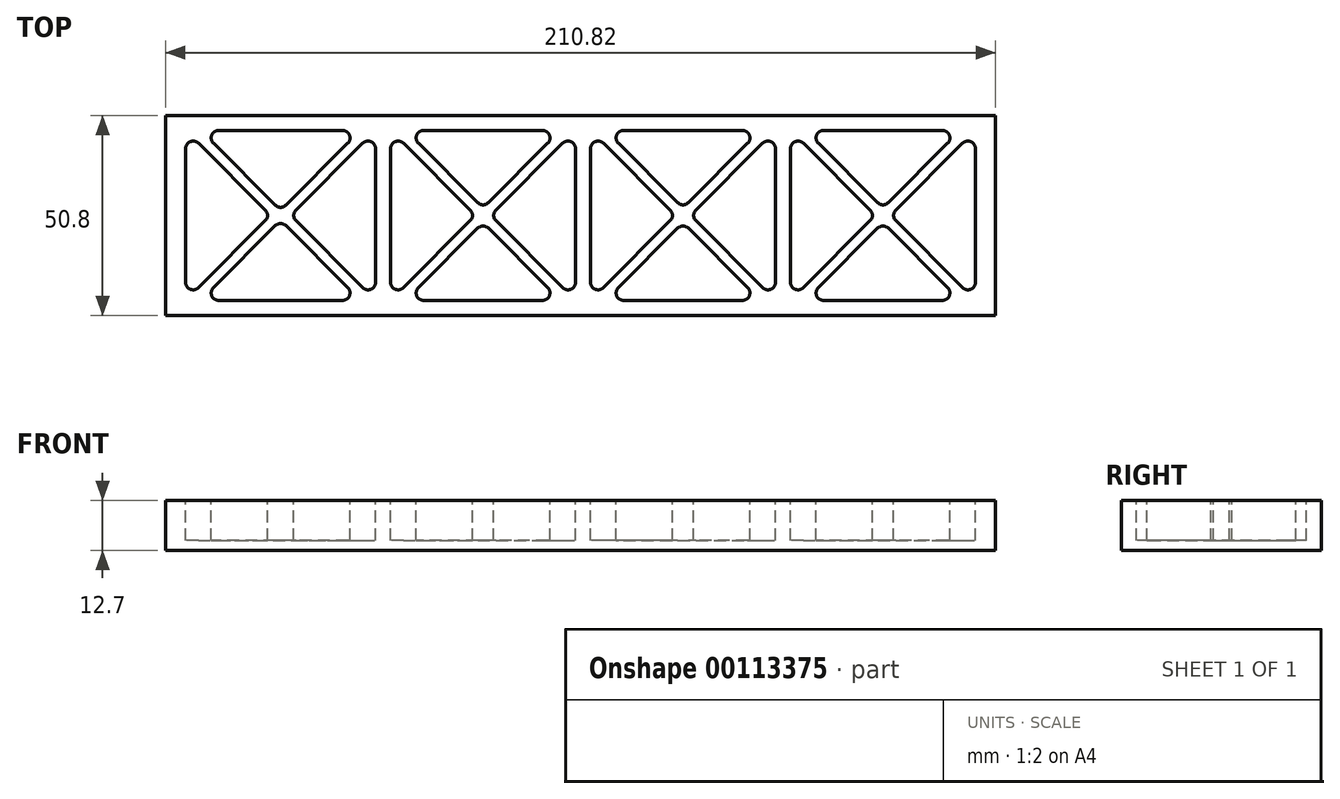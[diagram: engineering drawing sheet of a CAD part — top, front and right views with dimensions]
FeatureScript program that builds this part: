
annotation { "Feature Type Name" : "Feature", "Feature Type Description" : "" }
export const myFeature = defineFeature(function(context is Context, id is Id, definition is map)
    precondition{}
    {
        {
            var Q0;
            Q0=qCreatedBy(makeId("Top.planeOp"),FACE);
            var sketch = newSketch(context, id + "F0", { "sketchPlane" : qUnion([Q0])});
            skLineSegment(sketch, "E0.bottom", {"start": v(0, 0) * mm, "end": v(210.82, 0) * mm});
            skLineSegment(sketch, "E0.top", {"start": v(0, 50.8) * mm, "end": v(210.82, 50.8) * mm});
            skLineSegment(sketch, "E0.left", {"start": v(0, 0) * mm, "end": v(0, 50.8) * mm});
            skLineSegment(sketch, "E0.right", {"start": v(210.82, 0) * mm, "end": v(210.82, 50.8) * mm});
            skSolve(sketch);
        }
        {
            var Q0;
            Q0 = qSketchRegion(id + "F0", true);
            extrude(context, id + "F1", {"entities" : qUnion([Q0]), "depth" : 12.7 * mm, "offsetDistance" : 25.4 * mm});
        }
        {
            var Q0;
            Q0=makeQuery(id+"F1.opExtrude","CAP_FACE",FACE,{"disambiguationData":[OSD([sQuery(id+"F0.wireOp",EDGE,"E0.bottom"),sQuery(id+"F0.wireOp",EDGE,"E0.top"),sQuery(id+"F0.wireOp",EDGE,"E0.left"),sQuery(id+"F0.wireOp",EDGE,"E0.right")])],"isStart":false});
            var sketch = newSketch(context, id + "F2", { "sketchPlane" : qUnion([Q0])});
            skLineSegment(sketch, "E1", {"start": v(0, 25.4) * mm, "end": v(210.82, 25.4) * mm, "construction": true});
            skLineSegment(sketch, "E2", {"start": v(5.08, 42.4) * mm, "end": v(5.08, 8.4) * mm});
            skLineSegment(sketch, "E3", {"start": v(8.33, 7.06) * mm, "end": v(25.32, 24.05) * mm});
            skLineSegment(sketch, "E4", {"start": v(25.32, 26.75) * mm, "end": v(8.33, 43.74) * mm});
            skLineSegment(sketch, "E5", {"start": v(33.1, 26.75) * mm, "end": v(50.09, 43.74) * mm});
            skLineSegment(sketch, "E6", {"start": v(53.34, 42.4) * mm, "end": v(53.34, 8.4) * mm});
            skLineSegment(sketch, "E7", {"start": v(50.09, 7.06) * mm, "end": v(33.1, 24.05) * mm});
            skLineSegment(sketch, "E8", {"start": v(57.15, 42.4) * mm, "end": v(57.15, 8.4) * mm});
            skLineSegment(sketch, "E9", {"start": v(60.4, 7.06) * mm, "end": v(77.4, 24.05) * mm});
            skLineSegment(sketch, "E10", {"start": v(77.4, 26.75) * mm, "end": v(60.4, 43.74) * mm});
            skLineSegment(sketch, "E11", {"start": v(104.14, 42.4) * mm, "end": v(104.14, 8.4) * mm});
            skLineSegment(sketch, "E12", {"start": v(100.89, 7.06) * mm, "end": v(83.9, 24.05) * mm});
            skLineSegment(sketch, "E13", {"start": v(83.9, 26.75) * mm, "end": v(100.89, 43.74) * mm});
            skLineSegment(sketch, "E14", {"start": v(107.95, 42.4) * mm, "end": v(107.95, 8.4) * mm});
            skLineSegment(sketch, "E15", {"start": v(111.2, 7.06) * mm, "end": v(128.2, 24.05) * mm});
            skLineSegment(sketch, "E16", {"start": v(128.2, 26.75) * mm, "end": v(111.2, 43.74) * mm});
            skLineSegment(sketch, "E17", {"start": v(154.94, 42.4) * mm, "end": v(154.94, 8.4) * mm});
            skLineSegment(sketch, "E18", {"start": v(151.69, 7.06) * mm, "end": v(134.7, 24.05) * mm});
            skLineSegment(sketch, "E19", {"start": v(134.7, 26.75) * mm, "end": v(151.69, 43.74) * mm});
            skLineSegment(sketch, "E20", {"start": v(158.75, 42.4) * mm, "end": v(158.75, 8.4) * mm});
            skLineSegment(sketch, "E21", {"start": v(162, 7.06) * mm, "end": v(179, 24.05) * mm});
            skLineSegment(sketch, "E22", {"start": v(179, 26.75) * mm, "end": v(162, 43.74) * mm});
            skLineSegment(sketch, "E23", {"start": v(205.74, 42.4) * mm, "end": v(205.74, 8.4) * mm});
            skLineSegment(sketch, "E24", {"start": v(202.49, 7.06) * mm, "end": v(185.5, 24.05) * mm});
            skLineSegment(sketch, "E25", {"start": v(185.5, 26.75) * mm, "end": v(202.49, 43.74) * mm});
            skLineSegment(sketch, "E26", {"start": v(13.49, 46.99) * mm, "end": v(44.93, 46.99) * mm});
            skLineSegment(sketch, "E27", {"start": v(46.28, 43.74) * mm, "end": v(30.56, 28.02) * mm});
            skLineSegment(sketch, "E28", {"start": v(27.86, 28.02) * mm, "end": v(12.14, 43.74) * mm});
            skLineSegment(sketch, "E29", {"start": v(13.49, 3.8) * mm, "end": v(44.93, 3.8) * mm});
            skLineSegment(sketch, "E30", {"start": v(46.28, 7.06) * mm, "end": v(30.56, 22.78) * mm});
            skLineSegment(sketch, "E31", {"start": v(27.86, 22.78) * mm, "end": v(12.14, 7.06) * mm});
            skLineSegment(sketch, "E32", {"start": v(65.56, 46.99) * mm, "end": v(95.73, 46.99) * mm});
            skLineSegment(sketch, "E33", {"start": v(97.08, 43.74) * mm, "end": v(82, 28.65) * mm});
            skLineSegment(sketch, "E34", {"start": v(79.3, 28.65) * mm, "end": v(64.21, 43.74) * mm});
            skLineSegment(sketch, "E35", {"start": v(65.56, 3.8) * mm, "end": v(95.73, 3.8) * mm});
            skLineSegment(sketch, "E36", {"start": v(97.08, 7.06) * mm, "end": v(82, 22.15) * mm});
            skLineSegment(sketch, "E37", {"start": v(79.3, 22.15) * mm, "end": v(64.21, 7.06) * mm});
            skLineSegment(sketch, "E38", {"start": v(116.36, 46.99) * mm, "end": v(146.53, 46.99) * mm});
            skLineSegment(sketch, "E39", {"start": v(147.88, 43.74) * mm, "end": v(132.8, 28.65) * mm});
            skLineSegment(sketch, "E40", {"start": v(130.1, 28.65) * mm, "end": v(115.01, 43.74) * mm});
            skLineSegment(sketch, "E41", {"start": v(116.36, 3.8) * mm, "end": v(146.53, 3.8) * mm});
            skLineSegment(sketch, "E42", {"start": v(147.88, 7.06) * mm, "end": v(132.8, 22.15) * mm});
            skLineSegment(sketch, "E43", {"start": v(130.1, 22.15) * mm, "end": v(115.01, 7.06) * mm});
            skLineSegment(sketch, "E44", {"start": v(167.16, 46.99) * mm, "end": v(197.33, 46.99) * mm});
            skLineSegment(sketch, "E45", {"start": v(198.68, 43.74) * mm, "end": v(183.6, 28.65) * mm});
            skLineSegment(sketch, "E46", {"start": v(180.9, 28.65) * mm, "end": v(165.81, 43.74) * mm});
            skLineSegment(sketch, "E47", {"start": v(167.16, 3.8) * mm, "end": v(197.33, 3.8) * mm});
            skLineSegment(sketch, "E48", {"start": v(198.68, 7.06) * mm, "end": v(183.6, 22.15) * mm});
            skLineSegment(sketch, "E49", {"start": v(180.9, 22.15) * mm, "end": v(165.81, 7.06) * mm});
            skPoint(sketch, "E50.visualSharp", {"position": v(5.08, 46.99) * mm});
            skArc(sketch, "E50.filletArc", {"start": v(8.33, 43.74) * mm, "mid": v(6.26, 44.15) * mm, "end": v(5.08, 42.4) * mm});
            skPoint(sketch, "E51.visualSharp", {"position": v(5.08, 3.8) * mm});
            skArc(sketch, "E51.filletArc", {"start": v(5.08, 8.4) * mm, "mid": v(6.26, 6.65) * mm, "end": v(8.33, 7.06) * mm});
            skPoint(sketch, "E52.visualSharp", {"position": v(26.67, 25.4) * mm});
            skArc(sketch, "E52.filletArc", {"start": v(25.32, 24.05) * mm, "mid": v(25.88, 25.4) * mm, "end": v(25.32, 26.75) * mm});
            skPoint(sketch, "E53.visualSharp", {"position": v(8.89, 46.99) * mm});
            skArc(sketch, "E53.filletArc", {"start": v(13.49, 46.99) * mm, "mid": v(11.73, 45.81) * mm, "end": v(12.14, 43.74) * mm});
            skPoint(sketch, "E54.visualSharp", {"position": v(49.53, 46.99) * mm});
            skArc(sketch, "E54.filletArc", {"start": v(46.28, 43.74) * mm, "mid": v(46.7, 45.81) * mm, "end": v(44.93, 46.99) * mm});
            skPoint(sketch, "E55.visualSharp", {"position": v(29.21, 26.67) * mm});
            skArc(sketch, "E55.filletArc", {"start": v(27.86, 28.02) * mm, "mid": v(29.21, 27.46) * mm, "end": v(30.56, 28.02) * mm});
            skPoint(sketch, "E56.visualSharp", {"position": v(29.21, 24.13) * mm});
            skArc(sketch, "E56.filletArc", {"start": v(30.56, 22.78) * mm, "mid": v(29.21, 23.34) * mm, "end": v(27.86, 22.78) * mm});
            skPoint(sketch, "E57.visualSharp", {"position": v(8.9, 3.8) * mm});
            skArc(sketch, "E57.filletArc", {"start": v(12.14, 7.06) * mm, "mid": v(11.73, 4.99) * mm, "end": v(13.49, 3.8) * mm});
            skPoint(sketch, "E58.visualSharp", {"position": v(49.53, 3.8) * mm});
            skArc(sketch, "E58.filletArc", {"start": v(44.93, 3.8) * mm, "mid": v(46.7, 4.99) * mm, "end": v(46.28, 7.06) * mm});
            skPoint(sketch, "E59.visualSharp", {"position": v(31.75, 25.4) * mm});
            skArc(sketch, "E59.filletArc", {"start": v(33.1, 26.75) * mm, "mid": v(32.54, 25.4) * mm, "end": v(33.1, 24.05) * mm});
            skPoint(sketch, "E60.visualSharp", {"position": v(53.34, 46.99) * mm});
            skArc(sketch, "E60.filletArc", {"start": v(53.34, 42.4) * mm, "mid": v(52.16, 44.15) * mm, "end": v(50.09, 43.74) * mm});
            skPoint(sketch, "E61.visualSharp", {"position": v(53.34, 3.8) * mm});
            skArc(sketch, "E61.filletArc", {"start": v(50.09, 7.06) * mm, "mid": v(52.16, 6.65) * mm, "end": v(53.34, 8.4) * mm});
            skPoint(sketch, "E62.visualSharp", {"position": v(57.15, 46.99) * mm});
            skArc(sketch, "E62.filletArc", {"start": v(60.4, 43.74) * mm, "mid": v(58.33, 44.15) * mm, "end": v(57.15, 42.4) * mm});
            skPoint(sketch, "E63.visualSharp", {"position": v(57.15, 3.8) * mm});
            skArc(sketch, "E63.filletArc", {"start": v(57.15, 8.4) * mm, "mid": v(58.33, 6.65) * mm, "end": v(60.4, 7.06) * mm});
            skPoint(sketch, "E64.visualSharp", {"position": v(78.74, 25.4) * mm});
            skArc(sketch, "E64.filletArc", {"start": v(77.4, 24.05) * mm, "mid": v(77.95, 25.4) * mm, "end": v(77.4, 26.75) * mm});
            skPoint(sketch, "E65.visualSharp", {"position": v(60.96, 46.99) * mm});
            skArc(sketch, "E65.filletArc", {"start": v(65.56, 46.99) * mm, "mid": v(63.8, 45.81) * mm, "end": v(64.21, 43.74) * mm});
            skPoint(sketch, "E66.visualSharp", {"position": v(100.33, 46.99) * mm});
            skArc(sketch, "E66.filletArc", {"start": v(97.08, 43.74) * mm, "mid": v(97.5, 45.81) * mm, "end": v(95.73, 46.99) * mm});
            skPoint(sketch, "E67.visualSharp", {"position": v(80.64, 27.3) * mm});
            skArc(sketch, "E67.filletArc", {"start": v(79.3, 28.65) * mm, "mid": v(80.65, 28.1) * mm, "end": v(82, 28.65) * mm});
            skPoint(sketch, "E68.visualSharp", {"position": v(80.64, 23.5) * mm});
            skArc(sketch, "E68.filletArc", {"start": v(82, 22.15) * mm, "mid": v(80.65, 22.7) * mm, "end": v(79.3, 22.15) * mm});
            skPoint(sketch, "E69.visualSharp", {"position": v(60.96, 3.8) * mm});
            skArc(sketch, "E69.filletArc", {"start": v(64.21, 7.06) * mm, "mid": v(63.8, 4.99) * mm, "end": v(65.56, 3.8) * mm});
            skPoint(sketch, "E70.visualSharp", {"position": v(100.33, 3.8) * mm});
            skArc(sketch, "E70.filletArc", {"start": v(95.73, 3.8) * mm, "mid": v(97.5, 4.99) * mm, "end": v(97.08, 7.06) * mm});
            skPoint(sketch, "E71.visualSharp", {"position": v(82.55, 25.4) * mm});
            skArc(sketch, "E71.filletArc", {"start": v(83.9, 26.75) * mm, "mid": v(83.34, 25.4) * mm, "end": v(83.9, 24.05) * mm});
            skPoint(sketch, "E72.visualSharp", {"position": v(104.14, 46.99) * mm});
            skArc(sketch, "E72.filletArc", {"start": v(104.14, 42.4) * mm, "mid": v(102.96, 44.15) * mm, "end": v(100.89, 43.74) * mm});
            skPoint(sketch, "E73.visualSharp", {"position": v(104.14, 3.8) * mm});
            skArc(sketch, "E73.filletArc", {"start": v(100.89, 7.06) * mm, "mid": v(102.96, 6.65) * mm, "end": v(104.14, 8.4) * mm});
            skPoint(sketch, "E74.visualSharp", {"position": v(107.95, 46.99) * mm});
            skArc(sketch, "E74.filletArc", {"start": v(111.2, 43.74) * mm, "mid": v(109.13, 44.15) * mm, "end": v(107.95, 42.4) * mm});
            skPoint(sketch, "E75.visualSharp", {"position": v(129.54, 25.4) * mm});
            skArc(sketch, "E75.filletArc", {"start": v(128.2, 24.05) * mm, "mid": v(128.75, 25.4) * mm, "end": v(128.2, 26.75) * mm});
            skPoint(sketch, "E76.visualSharp", {"position": v(107.95, 3.8) * mm});
            skArc(sketch, "E76.filletArc", {"start": v(107.95, 8.4) * mm, "mid": v(109.13, 6.65) * mm, "end": v(111.2, 7.06) * mm});
            skPoint(sketch, "E77.visualSharp", {"position": v(111.76, 46.99) * mm});
            skArc(sketch, "E77.filletArc", {"start": v(116.36, 46.99) * mm, "mid": v(114.6, 45.81) * mm, "end": v(115.01, 43.74) * mm});
            skPoint(sketch, "E78.visualSharp", {"position": v(151.13, 46.99) * mm});
            skArc(sketch, "E78.filletArc", {"start": v(147.88, 43.74) * mm, "mid": v(148.3, 45.81) * mm, "end": v(146.53, 46.99) * mm});
            skPoint(sketch, "E79.visualSharp", {"position": v(131.44, 27.3) * mm});
            skArc(sketch, "E79.filletArc", {"start": v(130.1, 28.65) * mm, "mid": v(131.44, 28.1) * mm, "end": v(132.8, 28.65) * mm});
            skPoint(sketch, "E80.visualSharp", {"position": v(133.35, 25.4) * mm});
            skArc(sketch, "E80.filletArc", {"start": v(134.7, 26.75) * mm, "mid": v(134.14, 25.4) * mm, "end": v(134.7, 24.05) * mm});
            skPoint(sketch, "E81.visualSharp", {"position": v(154.94, 46.99) * mm});
            skArc(sketch, "E81.filletArc", {"start": v(154.94, 42.4) * mm, "mid": v(153.76, 44.15) * mm, "end": v(151.69, 43.74) * mm});
            skPoint(sketch, "E82.visualSharp", {"position": v(154.94, 3.8) * mm});
            skArc(sketch, "E82.filletArc", {"start": v(151.69, 7.06) * mm, "mid": v(153.76, 6.65) * mm, "end": v(154.94, 8.4) * mm});
            skPoint(sketch, "E83.visualSharp", {"position": v(131.44, 23.5) * mm});
            skArc(sketch, "E83.filletArc", {"start": v(132.8, 22.15) * mm, "mid": v(131.44, 22.7) * mm, "end": v(130.1, 22.15) * mm});
            skPoint(sketch, "E84.visualSharp", {"position": v(111.76, 3.8) * mm});
            skArc(sketch, "E84.filletArc", {"start": v(115.01, 7.06) * mm, "mid": v(114.6, 4.99) * mm, "end": v(116.36, 3.8) * mm});
            skPoint(sketch, "E85.visualSharp", {"position": v(151.13, 3.8) * mm});
            skArc(sketch, "E85.filletArc", {"start": v(146.53, 3.8) * mm, "mid": v(148.3, 4.99) * mm, "end": v(147.88, 7.06) * mm});
            skPoint(sketch, "E86.visualSharp", {"position": v(158.75, 46.99) * mm});
            skArc(sketch, "E86.filletArc", {"start": v(162, 43.74) * mm, "mid": v(159.93, 44.15) * mm, "end": v(158.75, 42.4) * mm});
            skPoint(sketch, "E87.visualSharp", {"position": v(158.75, 3.8) * mm});
            skArc(sketch, "E87.filletArc", {"start": v(158.75, 8.4) * mm, "mid": v(159.93, 6.65) * mm, "end": v(162, 7.06) * mm});
            skPoint(sketch, "E88.visualSharp", {"position": v(180.34, 25.4) * mm});
            skArc(sketch, "E88.filletArc", {"start": v(179, 24.05) * mm, "mid": v(179.55, 25.4) * mm, "end": v(179, 26.75) * mm});
            skPoint(sketch, "E89.visualSharp", {"position": v(162.56, 3.8) * mm});
            skArc(sketch, "E89.filletArc", {"start": v(165.81, 7.06) * mm, "mid": v(165.4, 4.99) * mm, "end": v(167.16, 3.8) * mm});
            skPoint(sketch, "E90.visualSharp", {"position": v(182.24, 23.5) * mm});
            skArc(sketch, "E90.filletArc", {"start": v(183.6, 22.15) * mm, "mid": v(182.24, 22.7) * mm, "end": v(180.9, 22.15) * mm});
            skPoint(sketch, "E91.visualSharp", {"position": v(201.93, 3.8) * mm});
            skArc(sketch, "E91.filletArc", {"start": v(197.33, 3.8) * mm, "mid": v(199.1, 4.99) * mm, "end": v(198.68, 7.06) * mm});
            skPoint(sketch, "E92.visualSharp", {"position": v(162.56, 46.99) * mm});
            skArc(sketch, "E92.filletArc", {"start": v(167.16, 46.99) * mm, "mid": v(165.4, 45.81) * mm, "end": v(165.81, 43.74) * mm});
            skPoint(sketch, "E93.visualSharp", {"position": v(201.93, 46.99) * mm});
            skArc(sketch, "E93.filletArc", {"start": v(198.68, 43.74) * mm, "mid": v(199.1, 45.81) * mm, "end": v(197.33, 46.99) * mm});
            skPoint(sketch, "E94.visualSharp", {"position": v(182.24, 27.3) * mm});
            skArc(sketch, "E94.filletArc", {"start": v(180.9, 28.65) * mm, "mid": v(182.24, 28.1) * mm, "end": v(183.6, 28.65) * mm});
            skPoint(sketch, "E95.visualSharp", {"position": v(184.15, 25.4) * mm});
            skArc(sketch, "E95.filletArc", {"start": v(185.5, 26.75) * mm, "mid": v(184.94, 25.4) * mm, "end": v(185.5, 24.05) * mm});
            skPoint(sketch, "E96.visualSharp", {"position": v(205.74, 46.99) * mm});
            skArc(sketch, "E96.filletArc", {"start": v(205.74, 42.4) * mm, "mid": v(204.56, 44.15) * mm, "end": v(202.49, 43.74) * mm});
            skPoint(sketch, "E97.visualSharp", {"position": v(205.74, 3.8) * mm});
            skArc(sketch, "E97.filletArc", {"start": v(202.49, 7.06) * mm, "mid": v(204.56, 6.65) * mm, "end": v(205.74, 8.4) * mm});
            skSolve(sketch);
        }
        {
            var Q0;
            Q0 = qSketchRegion(id + "F2", true);
            extrude(context, id + "F3", {"entities" : qUnion([Q0]), "operationType" : NewBodyOperationType.REMOVE, "oppositeDirection" : true, "depth" : 10.16 * mm, "offsetDistance" : 25.4 * mm});
        }
    });
